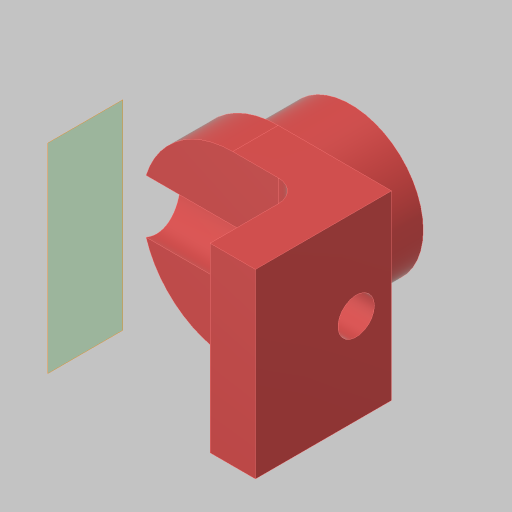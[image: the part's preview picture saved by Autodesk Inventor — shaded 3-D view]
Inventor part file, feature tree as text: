
AUTODESK INVENTOR PART (.ipt)
format: ipt  version: 2023.5 (Build 275446000, 446)  size: 177,152 bytes
history: native  units: in
note: dims shown in document units (in); Inventor stores cm internally (conversion verified against a paired STEP export)
features: sketch x6, extrude x4, projected_geometry x3, hole x2, fillet x1, plane x1
ambient origin geometry x8: Origin, YZ Plane, XZ Plane, XY Plane, X Axis, Y Axis, Z Axis, Center Point
bodies: Solid1 (feature_tree)
feature tree (17):
  extrude  "Extrusion1"  Depth=0.4in TaperAngle=0.0deg
  extrude  "Extrusion2"  Depth=0.25in TaperAngle=0.0deg
  hole  "Hole2"  [1 undecoded]
  extrude  "Extrusion3"  Depth=0.5in
  fillet  "Fillet1"  Radius=0.5in
  hole  "Hole3"  [1 undecoded]
  plane  "Work Plane1"
  extrude  "Extrusion4"  Depth=0.25in
  sketch  "Sketch1"  dims[d0=0.8in d1=0.4in d2=0.0in]
  sketch  "Sketch2"  dims[d3=0.1in d4=0.25in d5=0.0in]
  sketch  "Sketch4"  dims[d6=0.688in d14=0.625in]
  sketch  "Sketch5"  dims[d15=0.257in d16=0.75in d17=0.375in d18=0.25in d19=0.5635in d20=1.0in d21=0.8108in d22=0.25in d23=0.5in d24=0.0in]
  sketch  "Sketch6"  dims[d25=0.125in d26=0.5in]
  sketch  "Sketch7"  dims[d27=0.201in d28=0.38in d29=0.385in d30=0.25in d31=0.5635in d32=1.0in d33=0.8108in d34=0.25in d35=1.0in d36=0.555in d37=0.875in d38=0.315in d39=0.8in d40=0.0in]
  projected_geometry  "Project Cut Edges1"
  projected_geometry  "Project Cut Edges2"
  projected_geometry  "Project Cut Edges3"
note: 2 required parameter values undecoded (feature->parameter linkage not recoverable at this tier; creation-order binding heuristic only, values carry confidence <= 0.55)
